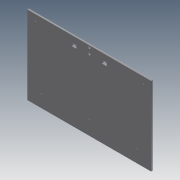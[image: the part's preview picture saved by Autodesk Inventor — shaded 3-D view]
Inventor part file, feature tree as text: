
AUTODESK INVENTOR PART (.ipt)
format: ipt  version: 2011 (Build 150239000, 239)  size: 440,320 bytes
history: native  units: in
note: dims shown in document units (in); Inventor stores cm internally (conversion verified against a paired STEP export)
features: extrude x23, sketch x23
ambient origin geometry x8: Origin, YZ Plane, XZ Plane, XY Plane, X Axis, Y Axis, Z Axis, Center Point
bodies: Solid1 (feature_tree)
feature tree (46):
  extrude  "Extrusion1"  Depth=12.85in
  extrude  "Extrusion2"  Depth=0.75in
  extrude  "Extrusion3"  Depth=2.0in
  extrude  "Extrusion4"  Depth=2.0in
  extrude  "Extrusion5"  Depth=2.0in
  extrude  "Extrusion6"  Depth=2.0in
  extrude  "Extrusion7"  Depth=2.0in
  extrude  "Extrusion8"  Depth=0.75in
  extrude  "Extrusion9"  Depth=0.25in TaperAngle=0.0deg
  extrude  "Extrusion10"  Depth=2.0in
  extrude  "Extrusion11"  Depth=7.175in
  extrude  "Extrusion12"  Depth=2.0in
  extrude  "Extrusion13"  Depth=2.0in
  extrude  "Extrusion14"  Depth=2.0in
  extrude  "Extrusion15"  Depth=0.25in TaperAngle=0.0deg
  extrude  "Extrusion16"  Depth=3.0in
  extrude  "Extrusion17"  Depth=3.0in
  extrude  "Extrusion18"  Depth=2.0in
  extrude  "Extrusion19"  Depth=1.0in TaperAngle=0.0deg
  extrude  "Extrusion20"  Depth=0.25in TaperAngle=0.0deg
  extrude  "Extrusion21"  Depth=0.25in TaperAngle=0.0deg
  extrude  "Extrusion22"  Depth=3.25in
  extrude  "Extrusion23"  Depth=2.0in
  sketch  "Sketch1"  dims[d0=19.5in d1=12.85in]
  sketch  "Sketch2"  dims[d2=0.25in d3=0.0in d4=0.75in]
  sketch  "Sketch3"  dims[d5=0.25in d6=2.0in]
  sketch  "Sketch4"  dims[d7=2.0in d8=2.0in]
  sketch  "Sketch5"  dims[d9=2.0in d10=2.0in]
  sketch  "Sketch6"  dims[d11=2.0in d12=2.0in]
  sketch  "Sketch7"  dims[d13=2.0in d14=2.0in]
  sketch  "Sketch8"  dims[d15=0.25in d16=0.0in d17=0.75in]
  sketch  "Sketch9"  dims[d18=0.25in d19=0.25in d20=0.0in]
  sketch  "Sketch10"  dims[d21=2.0in d22=2.0in]
  sketch  "Sketch12"  dims[d23=0.25in d24=0.0in d25=7.175in]
  sketch  "Sketch13"  dims[d26=0.25in d27=2.0in]
  sketch  "Sketch14"  dims[d28=2.0in d29=2.0in]
  sketch  "Sketch15"  dims[d30=2.0in d31=2.0in]
  sketch  "Sketch16"  dims[d32=0.25in d33=0.25in d34=0.0in]
  sketch  "Sketch17"  dims[d35=0.25in d36=0.0in d37=3.0in]
  sketch  "Sketch18"  dims[d38=3.0in d39=3.0in]
  sketch  "Sketch19"  dims[d40=3.0in d41=2.0in]
  sketch  "Sketch20"  dims[d42=2.0in d43=1.0in d44=0.0in]
  sketch  "Sketch21"  dims[d45=0.25in d46=0.0in d47=0.25in d48=0.0in]
  sketch  "Sketch22"  dims[d49=0.25in d50=0.0in d51=0.25in d52=0.0in]
  sketch  "Sketch23"  dims[d53=3.5in d54=3.25in]
  sketch  "Sketch24"  dims[d55=3.25in d56=2.0in d57=2.0in d58=0.25in d59=0.0in d60=0.25in d61=0.0in d62=3.25in d63=3.438in d64=3.25in d65=3.438in d66=2.0in d67=2.0in d68=0.25in d69=0.0in d70=1.25in d71=1.0in d72=2.25in d73=2.25in d74=1.25in d75=2.25in d76=0.156in d77=0.156in d78=0.156in d79=0.156in d80=1.0in d81=0.0in d82=10.35in d83=1.0in d84=1.0in d85=1.0in d86=0.156in d87=0.156in d88=1.0in d89=0.0in d90=0.25in d91=0.0in d92=10.35in d93=1.0in d94=1.0in d95=0.156in d96=0.25in d97=0.0in d98=0.315in d99=1.1811in d100=0.3937in d101=0.3937in d102=0.25in d103=0.0in d104=1.5in d105=1.0in d106=2.0in d107=1.0in d108=1.0in d109=0.75in d110=0.5in d111=0.75in d112=0.5in d113=0.25in d114=0.0in d115=10.105in d116=0.156in d117=0.25in d118=0.0in d119=0.25in d120=0.0in d121=3.25in d122=3.5in d123=3.25in d124=2.0in d125=2.0in d126=0.25in d127=0.0in]
